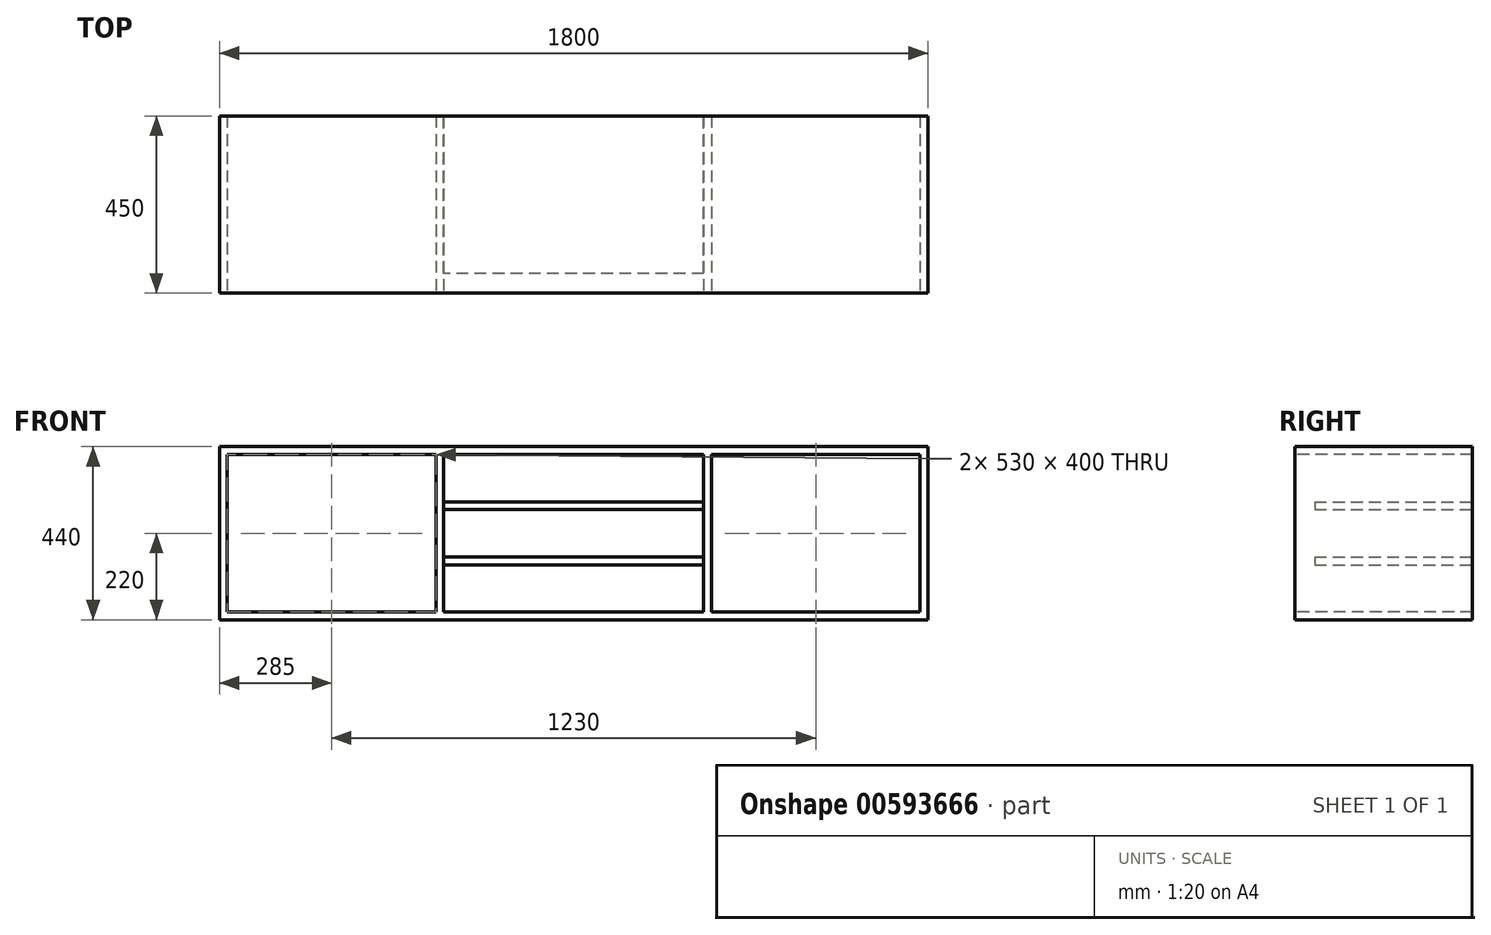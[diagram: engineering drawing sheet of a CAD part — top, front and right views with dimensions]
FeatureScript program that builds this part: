
annotation { "Feature Type Name" : "Feature", "Feature Type Description" : "" }
export const myFeature = defineFeature(function(context is Context, id is Id, definition is map)
    precondition{}
    {
        {
            var Q0;
            Q0=qCreatedBy(makeId("Top.planeOp"),FACE);
            var sketch = newSketch(context, id + "F0", { "sketchPlane" : qUnion([Q0])});
            skLineSegment(sketch, "E0.bottom", {"start": v(-900, 225) * mm, "end": v(900, 225) * mm});
            skLineSegment(sketch, "E0.top", {"start": v(-900, -225) * mm, "end": v(900, -225) * mm});
            skLineSegment(sketch, "E0.left", {"start": v(-900, 225) * mm, "end": v(-900, -225) * mm});
            skLineSegment(sketch, "E0.right", {"start": v(900, 225) * mm, "end": v(900, -225) * mm});
            skPoint(sketch, "E0.middle", {"position": v(0, 0) * mm});
            skSolve(sketch);
        }
        {
            var Q0;
            Q0=makeQuery(id+"F0.imprint","IMPRINT",FACE,{"disambiguationData":[TD([[makeQuery(id+"F0.imprint","IMPRINT",EDGE,{"derivedFrom":sQuery(id+"F0.wireOp",EDGE,"E0.bottom")}),-1.0]])]});
            extrude(context, id + "F1", {"entities" : qUnion([Q0]), "depth" : 20 * mm, "offsetDistance" : 25 * mm});
        }
        {
            var Q0;
            Q0=makeQuery(id+"F1.opExtrude","CAP_FACE",FACE,{"disambiguationData":[OSD([sQuery(id+"F0.wireOp",EDGE,"E0.bottom"),sQuery(id+"F0.wireOp",EDGE,"E0.top"),sQuery(id+"F0.wireOp",EDGE,"E0.left"),sQuery(id+"F0.wireOp",EDGE,"E0.right")])],"isStart":false});
            var sketch = newSketch(context, id + "F2", { "sketchPlane" : qUnion([Q0])});
            skLineSegment(sketch, "E1.bottom", {"start": v(-900, 225) * mm, "end": v(-880, 225) * mm});
            skLineSegment(sketch, "E1.top", {"start": v(-900, -225) * mm, "end": v(-880, -225) * mm});
            skLineSegment(sketch, "E1.left", {"start": v(-900, 225) * mm, "end": v(-900, -225) * mm});
            skLineSegment(sketch, "E1.right", {"start": v(-880, 225) * mm, "end": v(-880, -225) * mm});
            skLineSegment(sketch, "E2.bottom", {"start": v(900, 225) * mm, "end": v(880, 225) * mm});
            skLineSegment(sketch, "E2.top", {"start": v(900, -225) * mm, "end": v(880, -225) * mm});
            skLineSegment(sketch, "E2.left", {"start": v(900, 225) * mm, "end": v(900, -225) * mm});
            skLineSegment(sketch, "E2.right", {"start": v(880, 225) * mm, "end": v(880, -225) * mm});
            skLineSegment(sketch, "E3.bottom", {"start": v(-350, 225) * mm, "end": v(-330, 225) * mm});
            skLineSegment(sketch, "E3.top", {"start": v(-350, -225) * mm, "end": v(-330, -225) * mm});
            skLineSegment(sketch, "E3.left", {"start": v(-350, 225) * mm, "end": v(-350, -225) * mm});
            skLineSegment(sketch, "E3.right", {"start": v(-330, 225) * mm, "end": v(-330, -225) * mm});
            skLineSegment(sketch, "E4.bottom", {"start": v(330, 225) * mm, "end": v(350, 225) * mm});
            skLineSegment(sketch, "E4.top", {"start": v(330, -225) * mm, "end": v(350, -225) * mm});
            skLineSegment(sketch, "E4.left", {"start": v(330, 225) * mm, "end": v(330, -225) * mm});
            skLineSegment(sketch, "E4.right", {"start": v(350, 225) * mm, "end": v(350, -225) * mm});
            skSolve(sketch);
        }
        {
            var Q0;
            Q0=makeQuery(id+"F2.imprint","IMPRINT",FACE,{"disambiguationData":[TD([[makeQuery(id+"F2.imprint","IMPRINT",EDGE,{"derivedFrom":sQuery(id+"F2.wireOp",EDGE,"E1.bottom")}),-1.0]])]});
            var Q1;
            Q1=makeQuery(id+"F2.imprint","IMPRINT",FACE,{"disambiguationData":[TD([[makeQuery(id+"F2.imprint","IMPRINT",EDGE,{"derivedFrom":sQuery(id+"F2.wireOp",EDGE,"E2.bottom")}),-1.0]])]});
            var Q2;
            Q2=makeQuery(id+"F2.imprint","IMPRINT",FACE,{"disambiguationData":[TD([[makeQuery(id+"F2.imprint","IMPRINT",EDGE,{"derivedFrom":sQuery(id+"F2.wireOp",EDGE,"E4.bottom")}),-1.0]])]});
            var Q3;
            Q3=makeQuery(id+"F2.imprint","IMPRINT",FACE,{"disambiguationData":[TD([[makeQuery(id+"F2.imprint","IMPRINT",EDGE,{"derivedFrom":sQuery(id+"F2.wireOp",EDGE,"E3.bottom")}),-1.0]])]});
            extrude(context, id + "F3", {"entities" : qUnion([Q0, Q1, Q2, Q3]), "operationType" : NewBodyOperationType.ADD, "depth" : 400 * mm, "offsetDistance" : 25 * mm});
        }
        {
            var Q0;
            Q0=makeQuery(id+"F3.opExtrude","CAP_FACE",FACE,{"disambiguationData":[OSD([sQuery(id+"F2.wireOp",EDGE,"E2.bottom"),sQuery(id+"F2.wireOp",EDGE,"E2.top"),sQuery(id+"F2.wireOp",EDGE,"E2.left"),sQuery(id+"F2.wireOp",EDGE,"E2.right")])],"isStart":false});
            var sketch = newSketch(context, id + "F4", { "sketchPlane" : qUnion([Q0])});
            skLineSegment(sketch, "E5.left", {"start": v(900, -225) * mm, "end": v(900, 225) * mm});
            skLineSegment(sketch, "E6.bottom", {"start": v(-900, -225) * mm, "end": v(900, -225) * mm});
            skLineSegment(sketch, "E6.top", {"start": v(-900, 225) * mm, "end": v(900, 225) * mm});
            skLineSegment(sketch, "E6.left", {"start": v(-900, -225) * mm, "end": v(-900, 225) * mm});
            skPoint(sketch, "E6.middle", {"position": v(0, 0) * mm});
            skSolve(sketch);
        }
        {
            var Q0;
            {var subQ2=sQuery(id+"F4.wireOp",EDGE,"E6.left");Q0=makeQuery(id+"F4.imprint","IMPRINT",FACE,{"disambiguationData":[TD([[makeQuery(id+"F4.imprint","IMPRINT",EDGE,{"derivedFrom":subQ2}),-1.0]])]});}
            var Q1;
            {var subQ0=sQuery(id+"F4.wireOp",EDGE,"E5.left");Q1=makeQuery(id+"F4.imprint","IMPRINT",FACE,{"disambiguationData":[TD([[makeQuery(id+"F4.imprint","IMPRINT",EDGE,{"derivedFrom":subQ0}),-1.0]])]});}
            extrude(context, id + "F5", {"entities" : qUnion([Q0, Q1]), "operationType" : NewBodyOperationType.ADD, "depth" : 20 * mm, "offsetDistance" : 25 * mm});
        }
        {
            var Q0;
            Q0=makeQuery(id+"F3.opExtrude","SWEPT_FACE",FACE,{"disambiguationData":[OSD([sQuery(id+"F2.wireOp",EDGE,"E3.right")])]});
            var sketch = newSketch(context, id + "F6", { "sketchPlane" : qUnion([Q0])});
            skLineSegment(sketch, "E7.bottom", {"start": v(-175, 300) * mm, "end": v(225, 300) * mm});
            skLineSegment(sketch, "E7.top", {"start": v(-175, 280) * mm, "end": v(225, 280) * mm});
            skLineSegment(sketch, "E7.left", {"start": v(-175, 300) * mm, "end": v(-175, 280) * mm});
            skLineSegment(sketch, "E7.right", {"start": v(225, 300) * mm, "end": v(225, 280) * mm});
            skLineSegment(sketch, "E8.bottom", {"start": v(-175, 160) * mm, "end": v(225, 160) * mm});
            skLineSegment(sketch, "E8.top", {"start": v(-175, 140) * mm, "end": v(225, 140) * mm});
            skLineSegment(sketch, "E8.left", {"start": v(-175, 160) * mm, "end": v(-175, 140) * mm});
            skLineSegment(sketch, "E8.right", {"start": v(225, 160) * mm, "end": v(225, 140) * mm});
            skSolve(sketch);
        }
        {
            var Q0;
            Q0=makeQuery(id+"F6.imprint","IMPRINT",FACE,{"disambiguationData":[TD([[makeQuery(id+"F6.imprint","IMPRINT",EDGE,{"derivedFrom":sQuery(id+"F6.wireOp",EDGE,"E8.bottom")}),-1.0]])]});
            var Q1;
            Q1=makeQuery(id+"F6.imprint","IMPRINT",FACE,{"disambiguationData":[TD([[makeQuery(id+"F6.imprint","IMPRINT",EDGE,{"derivedFrom":sQuery(id+"F6.wireOp",EDGE,"E7.bottom")}),-1.0]])]});
            extrude(context, id + "F7", {"entities" : qUnion([Q0, Q1]), "operationType" : NewBodyOperationType.ADD, "depth" : 660 * mm, "offsetDistance" : 25 * mm});
        }
    });
